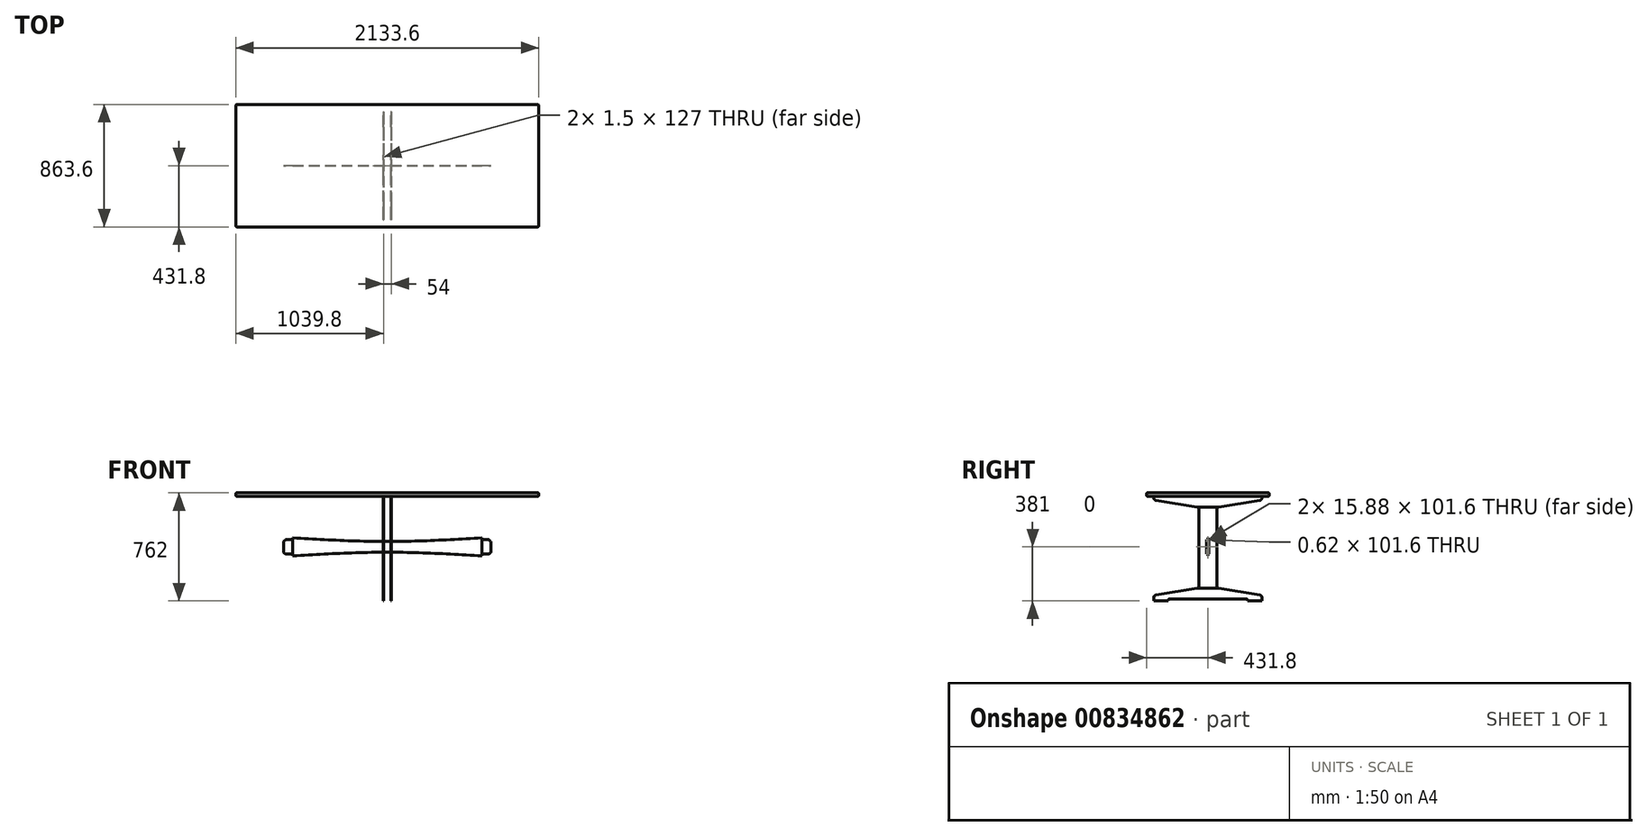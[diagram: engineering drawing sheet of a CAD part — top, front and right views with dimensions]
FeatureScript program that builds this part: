
annotation { "Feature Type Name" : "Feature", "Feature Type Description" : "" }
export const myFeature = defineFeature(function(context is Context, id is Id, definition is map)
    precondition{}
    {
        {
            assignVariable(context, id + "F0", {"name" : "legdepth", "anyValue" : 1.5});
        }
        {
            assignVariable(context, id + "F1", {"name" : "footdepth", "anyValue" : 2});
        }
        {
            assignVariable(context, id + "F2", {"name" : "stretcherdepth", "anyValue" : 1});
        }
        {
            assignVariable(context, id + "F3", {"name" : "tenondepth", "anyValue" : 5 / 8});
        }
        {
            assignVariable(context, id + "F4", {"name" : "legdistance", "anyValue" : 54});
        }
        {
            var Q0;
            Q0=qCreatedBy(makeId("Right.planeOp"),FACE);
            var sketch = newSketch(context, id + "F5", { "sketchPlane" : qUnion([Q0])});
            skLineSegment(sketch, "E0", {"start": v(0, 0) * mm, "end": v(0, 736.6) * mm});
            skLineSegment(sketch, "E1", {"start": v(0, 12.7) * mm, "end": v(-271.78, 12.7) * mm});
            skLineSegment(sketch, "E2", {"start": v(-279.4, 5.08) * mm, "end": v(-279.4, 0) * mm});
            skLineSegment(sketch, "E3", {"start": v(-279.4, 0) * mm, "end": v(-381, 0) * mm});
            skPoint(sketch, "E4.visualSharp", {"position": v(-279.4, 12.7) * mm});
            skArc(sketch, "E4.filletArc", {"start": v(-271.78, 12.7) * mm, "mid": v(-277.17, 10.47) * mm, "end": v(-279.4, 5.08) * mm});
            skPoint(sketch, "E5", {"position": v(0, 88.9) * mm});
            skPoint(sketch, "E6.MirrorP", {"position": v(0, 660.4) * mm});
            skLineSegment(sketch, "E7", {"start": v(0, 88.9) * mm, "end": v(-76.2, 88.9) * mm});
            skLineSegment(sketch, "E8", {"start": v(-381, 0) * mm, "end": v(-381, 23.04) * mm});
            skLineSegment(sketch, "E9", {"start": v(-366.14, 40.58) * mm, "end": v(-76.2, 88.9) * mm});
            skPoint(sketch, "E10.visualSharp", {"position": v(-381, 38.1) * mm});
            skArc(sketch, "E10.filletArc", {"start": v(-366.14, 40.58) * mm, "mid": v(-376.79, 34.53) * mm, "end": v(-381, 23.04) * mm});
            skLineSegment(sketch, "E11", {"start": v(-63.5, 88.9) * mm, "end": v(-63.5, 660.4) * mm});
            skLineSegment(sketch, "E12", {"start": v(0, 736.6) * mm, "end": v(-381, 736.6) * mm});
            skLineSegment(sketch, "E13", {"start": v(-381, 736.6) * mm, "end": v(-381, 726.26) * mm});
            skLineSegment(sketch, "E14", {"start": v(-366.14, 708.72) * mm, "end": v(-76.2, 660.4) * mm});
            skLineSegment(sketch, "E15", {"start": v(-76.2, 660.4) * mm, "end": v(0, 660.4) * mm});
            skPoint(sketch, "E16.visualSharp", {"position": v(-381, 711.2) * mm});
            skArc(sketch, "E16.filletArc", {"start": v(-381, 726.26) * mm, "mid": v(-376.79, 714.77) * mm, "end": v(-366.14, 708.72) * mm});
            skPoint(sketch, "E17", {"position": v(0, 381) * mm});
            skLineSegment(sketch, "E18", {"start": v(0, 431.8) * mm, "end": v(-7.94, 431.8) * mm});
            skLineSegment(sketch, "E19", {"start": v(-7.94, 431.8) * mm, "end": v(-7.94, 330.2) * mm});
            skLineSegment(sketch, "E20", {"start": v(-7.94, 330.2) * mm, "end": v(0, 330.2) * mm});
            skPoint(sketch, "E21", {"position": v(-7.94, 381) * mm});
            skSolve(sketch);
        }
        {
            var Q0;
            {var subQ0=sQuery(id+"F5.wireOp",EDGE,"E11");Q0=makeQuery(id+"F5.imprint","IMPRINT",FACE,{"disambiguationData":[TD([[makeQuery(id+"F5.imprint","IMPRINT",EDGE,{"derivedFrom":subQ0}),-1.0]])]});}
            extrude(context, id + "F6", {"entities" : qUnion([Q0]), "endBound" : BoundingType.SYMMETRIC, "depth" : (getVariable(context, 'legdepth')) * mm, "offsetDistance" : 25.4 * mm});
        }
        {
            var Q0;
            {var subQ1=sQuery(id+"F5.wireOp",EDGE,"E12");Q0=makeQuery(id+"F5.imprint","IMPRINT",FACE,{"disambiguationData":[TD([[makeQuery(id+"F5.imprint","IMPRINT",EDGE,{"derivedFrom":subQ1}),1.0]])]});}
            var Q1;
            {var subQ0=sQuery(id+"F5.wireOp",EDGE,"E1");Q1=makeQuery(id+"F5.imprint","IMPRINT",FACE,{"disambiguationData":[TD([[makeQuery(id+"F5.imprint","IMPRINT",EDGE,{"derivedFrom":subQ0}),-1.0]])]});}
            extrude(context, id + "F7", {"entities" : qUnion([Q0, Q1]), "operationType" : NewBodyOperationType.ADD, "endBound" : BoundingType.SYMMETRIC, "depth" : (getVariable(context, 'footdepth')) * mm, "offsetDistance" : 25 * mm});
        }
        {
            var Q0;
            Q0=makeQuery(id+"F6.opExtrude","SWEPT_BODY",BODY,{"disambiguationData":[OSD([sQuery(id+"F5.wireOp",EDGE,"E0"),sQuery(id+"F5.wireOp",EDGE,"E7"),sQuery(id+"F5.wireOp",EDGE,"E11"),sQuery(id+"F5.wireOp",EDGE,"E15"),sQuery(id+"F5.wireOp",EDGE,"E18"),sQuery(id+"F5.wireOp",EDGE,"E19"),sQuery(id+"F5.wireOp",EDGE,"E20")])]});
            var Q1;
            Q1=qCreatedBy(makeId("Front.planeOp"),FACE);
            mirror(context, id + "F8", {"operationType" : NewBodyOperationType.ADD, "entities" : qUnion([Q0]), "mirrorPlane" : qUnion([Q1])});
        }
        {
            var Q0;
            Q0=makeQuery(id+"F6.opExtrude","SWEPT_BODY",BODY,{"disambiguationData":[OSD([sQuery(id+"F5.wireOp",EDGE,"E0"),sQuery(id+"F5.wireOp",EDGE,"E7"),sQuery(id+"F5.wireOp",EDGE,"E11"),sQuery(id+"F5.wireOp",EDGE,"E15"),sQuery(id+"F5.wireOp",EDGE,"E18"),sQuery(id+"F5.wireOp",EDGE,"E19"),sQuery(id+"F5.wireOp",EDGE,"E20")])]});
            transform(context, id + "F9", {"entities" : qUnion([Q0]), "transformType" : TransformType.TRANSLATION_3D, "dx" : (getVariable(context, 'legdistance') / 2) * mm, "dy" : 0 * mm, "dz" : 0 * mm, "makeCopy" : false});
        }
        {
            var Q0;
            Q0=makeQuery(id+"F6.opExtrude","SWEPT_BODY",BODY,{"disambiguationData":[OSD([sQuery(id+"F5.wireOp",EDGE,"E0"),sQuery(id+"F5.wireOp",EDGE,"E7"),sQuery(id+"F5.wireOp",EDGE,"E11"),sQuery(id+"F5.wireOp",EDGE,"E15"),sQuery(id+"F5.wireOp",EDGE,"E18"),sQuery(id+"F5.wireOp",EDGE,"E19"),sQuery(id+"F5.wireOp",EDGE,"E20")])]});
            var Q1;
            Q1=qCreatedBy(makeId("Right.planeOp"),FACE);
            mirror(context, id + "F10", {"entities" : qUnion([Q0]), "mirrorPlane" : qUnion([Q1])});
        }
        {
            var Q0;
            {var subQ0=makeQuery(id+"F7.opExtrude","SWEPT_FACE",FACE,{"disambiguationData":[OSD([sQuery(id+"F5.wireOp",EDGE,"E12")])]});Q0=makeQuery(id+"F8.boolean.opBoolean","MERGE",FACE,{"derivedFrom":[subQ0,makeQuery(id+"F8.opPattern","COPY",FACE,{"derivedFrom":subQ0,"instanceName":"1"})]});}
            var sketch = newSketch(context, id + "F11", { "sketchPlane" : qUnion([Q0])});
            skLineSegment(sketch, "E22.bottom", {"start": v(1066.8, -431.8) * mm, "end": v(-1066.8, -431.8) * mm});
            skLineSegment(sketch, "E22.top", {"start": v(1066.8, 431.8) * mm, "end": v(-1066.8, 431.8) * mm});
            skLineSegment(sketch, "E22.left", {"start": v(1066.8, -431.8) * mm, "end": v(1066.8, 431.8) * mm});
            skLineSegment(sketch, "E22.right", {"start": v(-1066.8, -431.8) * mm, "end": v(-1066.8, 431.8) * mm});
            skPoint(sketch, "E22.middle", {"position": v(0, 0) * mm});
            skSolve(sketch);
        }
        {
            var Q0;
            Q0 = qSketchRegion(id + "F11", true);
            extrude(context, id + "F12", {"entities" : qUnion([Q0]), "depth" : 25.4 * mm, "offsetDistance" : 25.4 * mm});
        }
        {
            var Q0;
            Q0=qCreatedBy(makeId("Front.planeOp"),FACE);
            var sketch = newSketch(context, id + "F13", { "sketchPlane" : qUnion([Q0])});
            skLineSegment(sketch, "E23.bottom", {"start": v(666.75, 317.5) * mm, "end": v(-666.75, 317.5) * mm, "construction": true});
            skLineSegment(sketch, "E23.top", {"start": v(666.75, 444.5) * mm, "end": v(-666.75, 444.5) * mm, "construction": true});
            skLineSegment(sketch, "E23.left", {"start": v(666.75, 317.5) * mm, "end": v(666.75, 330.2) * mm});
            skLineSegment(sketch, "E23.right", {"start": v(-666.75, 317.5) * mm, "end": v(-666.75, 330.2) * mm});
            skPoint(sketch, "E23.middle", {"position": v(0, 381) * mm});
            skLineSegment(sketch, "E24.bottom", {"start": v(730.25, 330.2) * mm, "end": v(666.75, 330.2) * mm});
            skLineSegment(sketch, "E24.top", {"start": v(730.25, 431.8) * mm, "end": v(666.75, 431.8) * mm});
            skLineSegment(sketch, "E24.left", {"start": v(730.25, 330.2) * mm, "end": v(730.25, 431.8) * mm});
            skLineSegment(sketch, "E24.right", {"start": v(-730.25, 330.2) * mm, "end": v(-730.25, 431.8) * mm});
            skLineSegment(sketch, "E25.trimOffspring", {"start": v(-666.75, 431.8) * mm, "end": v(-730.25, 431.8) * mm});
            skLineSegment(sketch, "E26.trimOffspring", {"start": v(-666.75, 330.2) * mm, "end": v(-730.25, 330.2) * mm});
            skLineSegment(sketch, "E27.trimOffspring", {"start": v(666.75, 431.8) * mm, "end": v(666.75, 444.5) * mm});
            skLineSegment(sketch, "E28.trimOffspring", {"start": v(-666.75, 431.8) * mm, "end": v(-666.75, 444.5) * mm});
            skLineSegment(sketch, "E29", {"start": v(666.75, 431.8) * mm, "end": v(666.75, 330.2) * mm});
            skLineSegment(sketch, "E30", {"start": v(-666.75, 431.8) * mm, "end": v(-666.75, 330.2) * mm});
            skFitSpline(sketch, "E31", {"points": [v(-666.75, 444.5) * mm, v(0, 419.1) * mm, v(666.75, 444.5) * mm], "startDerivative": vector(1333.5, -83.59) * mm, "endDerivative": vector(1333.5, 83.59) * mm});
            skLineSegment(sketch, "E32", {"start": v(0, 381) * mm, "end": v(-124.6, 381) * mm, "construction": true});
            skFitSpline(sketch, "E33.MirrorCS", {"points": [v(-666.75, 317.5) * mm, v(0, 342.9) * mm, v(666.75, 317.5) * mm], "startDerivative": vector(1333.5, 83.59) * mm, "endDerivative": vector(1333.5, -83.59) * mm});
            skSolve(sketch);
        }
        {
            var Q0;
            Q0=makeQuery(id+"F13.imprint","IMPRINT",FACE,{"disambiguationData":[TD([[makeQuery(id+"F13.imprint","IMPRINT",EDGE,{"derivedFrom":sQuery(id+"F13.wireOp",EDGE,"E23.right")}),-1.0]])]});
            extrude(context, id + "F14", {"entities" : qUnion([Q0]), "endBound" : BoundingType.SYMMETRIC, "oppositeDirection" : true, "depth" : (getVariable(context, 'stretcherdepth')) * mm, "offsetDistance" : 25.4 * mm});
        }
        {
            var Q0;
            Q0=makeQuery(id+"F13.imprint","IMPRINT",FACE,{"disambiguationData":[TD([[makeQuery(id+"F13.imprint","IMPRINT",EDGE,{"derivedFrom":sQuery(id+"F13.wireOp",EDGE,"E24.bottom")}),-1.0]])]});
            var Q1;
            Q1=makeQuery(id+"F13.imprint","IMPRINT",FACE,{"disambiguationData":[TD([[makeQuery(id+"F13.imprint","IMPRINT",EDGE,{"derivedFrom":sQuery(id+"F13.wireOp",EDGE,"E24.right")}),-1.0]])]});
            extrude(context, id + "F15", {"entities" : qUnion([Q0, Q1]), "operationType" : NewBodyOperationType.ADD, "endBound" : BoundingType.SYMMETRIC, "depth" : (getVariable(context, 'tenondepth')) * mm, "offsetDistance" : 25.4 * mm});
        }
        {
            var Q0;
            Q0=makeQuery(id+"F15.opExtrude","SWEPT_EDGE",EDGE,{"disambiguationData":[OSD([sQuery(id+"F13.wireOp",EDGE,"E24.right"),sQuery(id+"F13.wireOp",EDGE,"E25.trimOffspring")])]});
            var Q1;
            Q1=makeQuery(id+"F15.opExtrude","SWEPT_EDGE",EDGE,{"disambiguationData":[OSD([sQuery(id+"F13.wireOp",EDGE,"E24.right"),sQuery(id+"F13.wireOp",EDGE,"E26.trimOffspring")])]});
            var Q2;
            Q2=makeQuery(id+"F15.opExtrude","SWEPT_EDGE",EDGE,{"disambiguationData":[OSD([sQuery(id+"F13.wireOp",EDGE,"E24.top"),sQuery(id+"F13.wireOp",EDGE,"E24.left")])]});
            var Q3;
            Q3=makeQuery(id+"F15.opExtrude","SWEPT_EDGE",EDGE,{"disambiguationData":[OSD([sQuery(id+"F13.wireOp",EDGE,"E24.bottom"),sQuery(id+"F13.wireOp",EDGE,"E24.left")])]});
            chamfer(context, id + "F16", {"entities" : qUnion([Q0, Q1, Q2, Q3]), "width" : 12.7 * mm, "tangentPropagation" : true});
        }
        {
            var Q0;
            {var subQ0=sQuery(id+"F13.wireOp",EDGE,"E24.top");Q0=makeQuery(id+"F16.opChamfer","BLEND_EDGE",EDGE,{"blendedFrom":[makeQuery(id+"F15.opExtrude","SWEPT_EDGE",EDGE,{"disambiguationData":[OSD([subQ0,sQuery(id+"F13.wireOp",EDGE,"E24.left")])]}),makeQuery(id+"F15.opExtrude","SWEPT_FACE",FACE,{"disambiguationData":[OSD([subQ0])]})],"blendedInto":[makeQuery(id+"F15.opExtrude","SWEPT_FACE",FACE,{"disambiguationData":[OSD([subQ0])]})]});}
            var Q1;
            {var subQ0=sQuery(id+"F13.wireOp",EDGE,"E24.left");Q1=makeQuery(id+"F16.opChamfer","BLEND_EDGE",EDGE,{"blendedFrom":[makeQuery(id+"F15.opExtrude","SWEPT_EDGE",EDGE,{"disambiguationData":[OSD([sQuery(id+"F13.wireOp",EDGE,"E24.top"),subQ0])]}),makeQuery(id+"F15.opExtrude","SWEPT_FACE",FACE,{"disambiguationData":[OSD([subQ0])]})],"blendedInto":[makeQuery(id+"F15.opExtrude","SWEPT_FACE",FACE,{"disambiguationData":[OSD([subQ0])]})]});}
            var Q2;
            {var subQ0=sQuery(id+"F13.wireOp",EDGE,"E24.left");Q2=makeQuery(id+"F16.opChamfer","BLEND_EDGE",EDGE,{"blendedFrom":[makeQuery(id+"F15.opExtrude","SWEPT_EDGE",EDGE,{"disambiguationData":[OSD([sQuery(id+"F13.wireOp",EDGE,"E24.bottom"),subQ0])]}),makeQuery(id+"F15.opExtrude","SWEPT_FACE",FACE,{"disambiguationData":[OSD([subQ0])]})],"blendedInto":[makeQuery(id+"F15.opExtrude","SWEPT_FACE",FACE,{"disambiguationData":[OSD([subQ0])]})]});}
            var Q3;
            {var subQ0=sQuery(id+"F13.wireOp",EDGE,"E24.bottom");Q3=makeQuery(id+"F16.opChamfer","BLEND_EDGE",EDGE,{"blendedFrom":[makeQuery(id+"F15.opExtrude","SWEPT_EDGE",EDGE,{"disambiguationData":[OSD([subQ0,sQuery(id+"F13.wireOp",EDGE,"E24.left")])]}),makeQuery(id+"F15.opExtrude","SWEPT_FACE",FACE,{"disambiguationData":[OSD([subQ0])]})],"blendedInto":[makeQuery(id+"F15.opExtrude","SWEPT_FACE",FACE,{"disambiguationData":[OSD([subQ0])]})]});}
            var Q4;
            {var subQ0=sQuery(id+"F13.wireOp",EDGE,"E25.trimOffspring");Q4=makeQuery(id+"F16.opChamfer","BLEND_EDGE",EDGE,{"blendedFrom":[makeQuery(id+"F15.opExtrude","SWEPT_EDGE",EDGE,{"disambiguationData":[OSD([sQuery(id+"F13.wireOp",EDGE,"E24.right"),subQ0])]}),makeQuery(id+"F15.opExtrude","SWEPT_FACE",FACE,{"disambiguationData":[OSD([subQ0])]})],"blendedInto":[makeQuery(id+"F15.opExtrude","SWEPT_FACE",FACE,{"disambiguationData":[OSD([subQ0])]})]});}
            var Q5;
            {var subQ0=sQuery(id+"F13.wireOp",EDGE,"E24.right");Q5=makeQuery(id+"F16.opChamfer","BLEND_EDGE",EDGE,{"blendedFrom":[makeQuery(id+"F15.opExtrude","SWEPT_EDGE",EDGE,{"disambiguationData":[OSD([subQ0,sQuery(id+"F13.wireOp",EDGE,"E25.trimOffspring")])]}),makeQuery(id+"F15.opExtrude","SWEPT_FACE",FACE,{"disambiguationData":[OSD([subQ0])]})],"blendedInto":[makeQuery(id+"F15.opExtrude","SWEPT_FACE",FACE,{"disambiguationData":[OSD([subQ0])]})]});}
            var Q6;
            {var subQ0=sQuery(id+"F13.wireOp",EDGE,"E24.right");Q6=makeQuery(id+"F16.opChamfer","BLEND_EDGE",EDGE,{"blendedFrom":[makeQuery(id+"F15.opExtrude","SWEPT_EDGE",EDGE,{"disambiguationData":[OSD([subQ0,sQuery(id+"F13.wireOp",EDGE,"E26.trimOffspring")])]}),makeQuery(id+"F15.opExtrude","SWEPT_FACE",FACE,{"disambiguationData":[OSD([subQ0])]})],"blendedInto":[makeQuery(id+"F15.opExtrude","SWEPT_FACE",FACE,{"disambiguationData":[OSD([subQ0])]})]});}
            var Q7;
            {var subQ0=sQuery(id+"F13.wireOp",EDGE,"E26.trimOffspring");Q7=makeQuery(id+"F16.opChamfer","BLEND_EDGE",EDGE,{"blendedFrom":[makeQuery(id+"F15.opExtrude","SWEPT_EDGE",EDGE,{"disambiguationData":[OSD([sQuery(id+"F13.wireOp",EDGE,"E24.right"),subQ0])]}),makeQuery(id+"F15.opExtrude","SWEPT_FACE",FACE,{"disambiguationData":[OSD([subQ0])]})],"blendedInto":[makeQuery(id+"F15.opExtrude","SWEPT_FACE",FACE,{"disambiguationData":[OSD([subQ0])]})]});}
            fillet(context, id + "F17", {"entities" : qUnion([Q0, Q1, Q2, Q3, Q4, Q5, Q6, Q7]), "radius" : 5.08 * mm, "tangentPropagation" : true, "allowEdgeOverflow" : false});
        }
        {
            var Q0;
            Q0=makeQuery(id+"F12.opExtrude","CAP_EDGE",EDGE,{"disambiguationData":[OSD([sQuery(id+"F11.wireOp",EDGE,"E22.bottom")])],"isStart":false});
            var Q1;
            Q1=makeQuery(id+"F12.opExtrude","CAP_EDGE",EDGE,{"disambiguationData":[OSD([sQuery(id+"F11.wireOp",EDGE,"E22.top")])],"isStart":false});
            var Q2;
            Q2=makeQuery(id+"F12.opExtrude","CAP_EDGE",EDGE,{"disambiguationData":[OSD([sQuery(id+"F11.wireOp",EDGE,"E22.right")])],"isStart":false});
            var Q3;
            Q3=makeQuery(id+"F12.opExtrude","CAP_EDGE",EDGE,{"disambiguationData":[OSD([sQuery(id+"F11.wireOp",EDGE,"E22.left")])],"isStart":false});
            var Q4;
            Q4=makeQuery(id+"F12.opExtrude","SWEPT_EDGE",EDGE,{"disambiguationData":[OSD([sQuery(id+"F11.wireOp",EDGE,"E22.bottom"),sQuery(id+"F11.wireOp",EDGE,"E22.right")])]});
            var Q5;
            Q5=makeQuery(id+"F12.opExtrude","SWEPT_EDGE",EDGE,{"disambiguationData":[OSD([sQuery(id+"F11.wireOp",EDGE,"E22.top"),sQuery(id+"F11.wireOp",EDGE,"E22.right")])]});
            var Q6;
            Q6=makeQuery(id+"F12.opExtrude","SWEPT_EDGE",EDGE,{"disambiguationData":[OSD([sQuery(id+"F11.wireOp",EDGE,"E22.top"),sQuery(id+"F11.wireOp",EDGE,"E22.left")])]});
            var Q7;
            Q7=makeQuery(id+"F12.opExtrude","SWEPT_EDGE",EDGE,{"disambiguationData":[OSD([sQuery(id+"F11.wireOp",EDGE,"E22.bottom"),sQuery(id+"F11.wireOp",EDGE,"E22.left")])]});
            var Q8;
            Q8=makeQuery(id+"F12.opExtrude","CAP_EDGE",EDGE,{"disambiguationData":[OSD([sQuery(id+"F11.wireOp",EDGE,"E22.left")])],"isStart":true});
            var Q9;
            Q9=makeQuery(id+"F12.opExtrude","CAP_EDGE",EDGE,{"disambiguationData":[OSD([sQuery(id+"F11.wireOp",EDGE,"E22.bottom")])],"isStart":true});
            var Q10;
            Q10=makeQuery(id+"F12.opExtrude","CAP_EDGE",EDGE,{"disambiguationData":[OSD([sQuery(id+"F11.wireOp",EDGE,"E22.right")])],"isStart":true});
            var Q11;
            Q11=makeQuery(id+"F12.opExtrude","CAP_EDGE",EDGE,{"disambiguationData":[OSD([sQuery(id+"F11.wireOp",EDGE,"E22.top")])],"isStart":true});
            fillet(context, id + "F18", {"entities" : qUnion([Q0, Q1, Q2, Q3, Q4, Q5, Q6, Q7, Q8, Q9, Q10, Q11]), "radius" : 7.62 * mm, "tangentPropagation" : true, "allowEdgeOverflow" : false});
        }
    });
